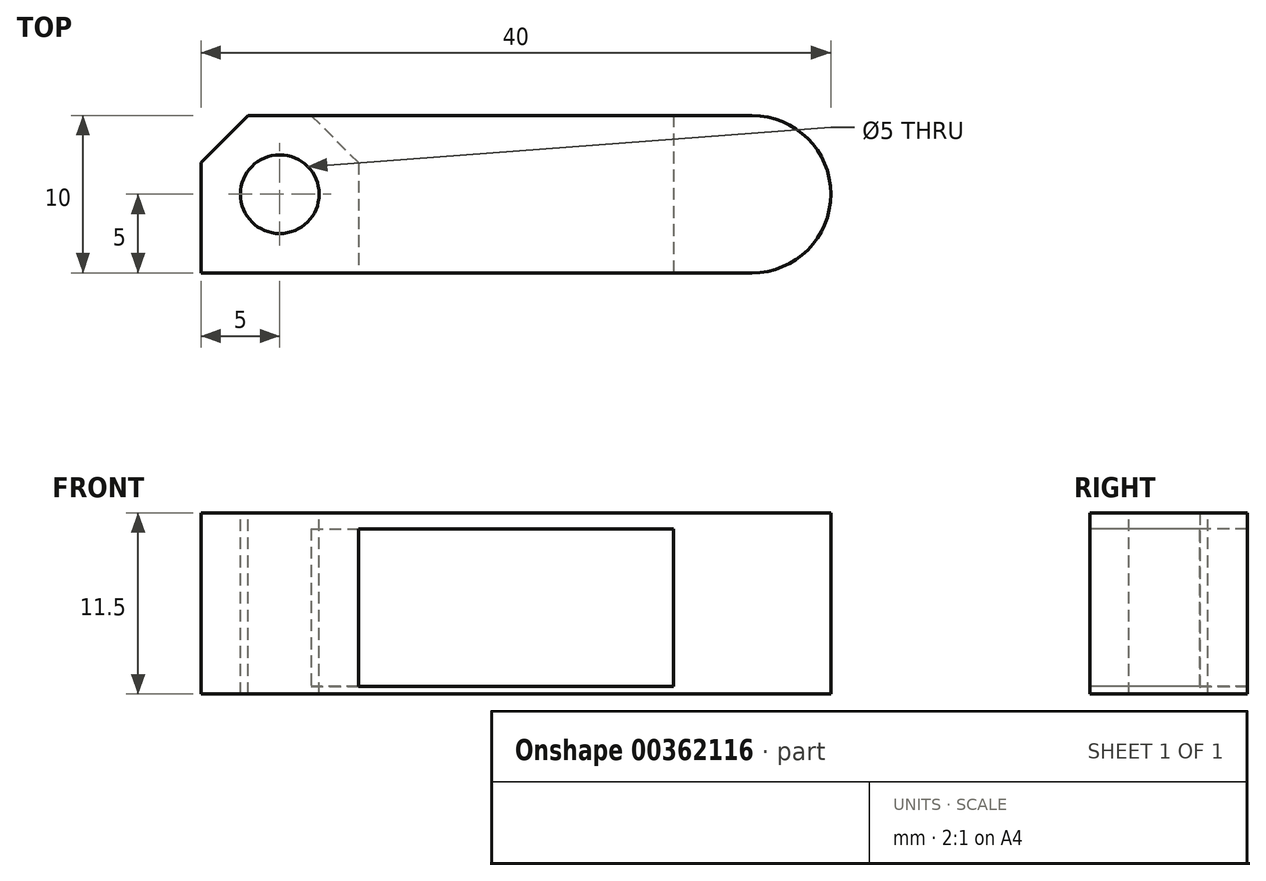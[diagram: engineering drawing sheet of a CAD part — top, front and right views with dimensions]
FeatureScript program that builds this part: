
annotation { "Feature Type Name" : "Feature", "Feature Type Description" : "" }
export const myFeature = defineFeature(function(context is Context, id is Id, definition is map)
    precondition{}
    {
        {
            var Q0;
            Q0=qCreatedBy(makeId("Top.planeOp"),FACE);
            var sketch = newSketch(context, id + "F0", { "sketchPlane" : qUnion([Q0])});
            skLineSegment(sketch, "E0.bottom", {"start": v(-20, 5) * mm, "end": v(20, 5) * mm});
            skLineSegment(sketch, "E0.top", {"start": v(-20, -5) * mm, "end": v(20, -5) * mm});
            skLineSegment(sketch, "E0.left", {"start": v(-20, 5) * mm, "end": v(-20, -5) * mm});
            skLineSegment(sketch, "E0.right", {"start": v(20, 5) * mm, "end": v(20, -5) * mm});
            skPoint(sketch, "E0.middle", {"position": v(0, 0) * mm});
            skSolve(sketch);
        }
        {
            var Q0;
            Q0=makeQuery(id+"F0.imprint","IMPRINT",FACE,{"disambiguationData":[TD([[makeQuery(id+"F0.imprint","IMPRINT",EDGE,{"derivedFrom":sQuery(id+"F0.wireOp",EDGE,"E0.bottom")}),-1.0]])]});
            extrude(context, id + "F1", {"entities" : qUnion([Q0]), "depth" : 0.5 * mm});
        }
        {
            var Q0;
            Q0=makeQuery(id+"F1.opExtrude","CAP_FACE",FACE,{"disambiguationData":[OSD([sQuery(id+"F0.wireOp",EDGE,"E0.bottom"),sQuery(id+"F0.wireOp",EDGE,"E0.top"),sQuery(id+"F0.wireOp",EDGE,"E0.left"),sQuery(id+"F0.wireOp",EDGE,"E0.right")])],"isStart":false});
            var sketch = newSketch(context, id + "F2", { "sketchPlane" : qUnion([Q0])});
            skLineSegment(sketch, "E1.bottom", {"start": v(-20, 5) * mm, "end": v(-10, 5) * mm});
            skLineSegment(sketch, "E1.top", {"start": v(-20, -5) * mm, "end": v(-10, -5) * mm});
            skLineSegment(sketch, "E1.left", {"start": v(-20, 5) * mm, "end": v(-20, -5) * mm});
            skLineSegment(sketch, "E1.right", {"start": v(-10, 5) * mm, "end": v(-10, -5) * mm});
            skLineSegment(sketch, "E2.bottom", {"start": v(20, 5) * mm, "end": v(10, 5) * mm});
            skLineSegment(sketch, "E2.top", {"start": v(20, -5) * mm, "end": v(10, -5) * mm});
            skLineSegment(sketch, "E2.left", {"start": v(20, 5) * mm, "end": v(20, -5) * mm});
            skLineSegment(sketch, "E2.right", {"start": v(10, 5) * mm, "end": v(10, -5) * mm});
            skSolve(sketch);
        }
        {
            var Q0;
            Q0=makeQuery(id+"F2.imprint","IMPRINT",FACE,{"disambiguationData":[TD([[makeQuery(id+"F2.imprint","IMPRINT",EDGE,{"derivedFrom":sQuery(id+"F2.wireOp",EDGE,"E1.bottom")}),-1.0]])]});
            var Q1;
            Q1=makeQuery(id+"F2.imprint","IMPRINT",FACE,{"disambiguationData":[TD([[makeQuery(id+"F2.imprint","IMPRINT",EDGE,{"derivedFrom":sQuery(id+"F2.wireOp",EDGE,"E2.bottom")}),-1.0]])]});
            extrude(context, id + "F3", {"entities" : qUnion([Q0, Q1]), "operationType" : NewBodyOperationType.ADD, "depth" : 10 * mm});
        }
        {
            var Q0;
            Q0=makeQuery(id+"F3.opExtrude","CAP_FACE",FACE,{"disambiguationData":[OSD([sQuery(id+"F2.wireOp",EDGE,"E1.bottom"),sQuery(id+"F2.wireOp",EDGE,"E1.top"),sQuery(id+"F2.wireOp",EDGE,"E1.left"),sQuery(id+"F2.wireOp",EDGE,"E1.right")])],"isStart":false});
            var sketch = newSketch(context, id + "F4", { "sketchPlane" : qUnion([Q0])});
            skLineSegment(sketch, "E3.bottom", {"start": v(-20, -5) * mm, "end": v(20, -5) * mm});
            skLineSegment(sketch, "E3.top", {"start": v(-20, 5) * mm, "end": v(20, 5) * mm});
            skLineSegment(sketch, "E3.left", {"start": v(-20, -5) * mm, "end": v(-20, 5) * mm});
            skLineSegment(sketch, "E3.right", {"start": v(20, -5) * mm, "end": v(20, 5) * mm});
            skSolve(sketch);
        }
        {
            var Q0;
            {var subQ0=sQuery(id+"F4.wireOp",EDGE,"E3.left");Q0=makeQuery(id+"F4.imprint","IMPRINT",FACE,{"disambiguationData":[TD([[makeQuery(id+"F4.imprint","IMPRINT",EDGE,{"derivedFrom":subQ0}),1.0]])]});}
            var Q1;
            {var subQ2=sQuery(id+"F4.wireOp",EDGE,"E3.right");Q1=makeQuery(id+"F4.imprint","IMPRINT",FACE,{"disambiguationData":[TD([[makeQuery(id+"F4.imprint","IMPRINT",EDGE,{"derivedFrom":subQ2}),1.0]])]});}
            extrude(context, id + "F5", {"entities" : qUnion([Q0, Q1]), "operationType" : NewBodyOperationType.ADD, "depth" : 1 * mm});
        }
        {
            var Q0;
            Q0=makeQuery(id+"F5.boolean.opBoolean","MERGE",EDGE,{"derivedFrom":[makeQuery(id+"F3.boolean.opBoolean","MERGE",EDGE,{"derivedFrom":[makeQuery(id+"F1.opExtrude","SWEPT_EDGE",EDGE,{"disambiguationData":[OSD([sQuery(id+"F0.wireOp",EDGE,"E0.top"),sQuery(id+"F0.wireOp",EDGE,"E0.right")])]}),makeQuery(id+"F3.opExtrude","SWEPT_EDGE",EDGE,{"disambiguationData":[OSD([sQuery(id+"F2.wireOp",EDGE,"E2.top"),sQuery(id+"F2.wireOp",EDGE,"E2.left")])]})]}),makeQuery(id+"F5.opExtrude","SWEPT_EDGE",EDGE,{"disambiguationData":[OSD([sQuery(id+"F4.wireOp",EDGE,"E3.bottom"),sQuery(id+"F4.wireOp",EDGE,"E3.right")])]})]});
            var Q1;
            Q1=makeQuery(id+"F5.boolean.opBoolean","MERGE",EDGE,{"derivedFrom":[makeQuery(id+"F3.boolean.opBoolean","MERGE",EDGE,{"derivedFrom":[makeQuery(id+"F1.opExtrude","SWEPT_EDGE",EDGE,{"disambiguationData":[OSD([sQuery(id+"F0.wireOp",EDGE,"E0.bottom"),sQuery(id+"F0.wireOp",EDGE,"E0.right")])]}),makeQuery(id+"F3.opExtrude","SWEPT_EDGE",EDGE,{"disambiguationData":[OSD([sQuery(id+"F2.wireOp",EDGE,"E2.bottom"),sQuery(id+"F2.wireOp",EDGE,"E2.left")])]})]}),makeQuery(id+"F5.opExtrude","SWEPT_EDGE",EDGE,{"disambiguationData":[OSD([sQuery(id+"F4.wireOp",EDGE,"E3.top"),sQuery(id+"F4.wireOp",EDGE,"E3.right")])]})]});
            fillet(context, id + "F6", {"entities" : qUnion([Q0, Q1]), "radius" : 5 * mm, "tangentPropagation" : true, "allowEdgeOverflow" : false});
        }
        {
            var Q0;
            Q0=makeQuery(id+"F5.opExtrude","CAP_FACE",FACE,{"disambiguationData":[OSD([sQuery(id+"F4.wireOp",EDGE,"E3.bottom"),sQuery(id+"F4.wireOp",EDGE,"E3.top"),sQuery(id+"F4.wireOp",EDGE,"E3.left"),sQuery(id+"F4.wireOp",EDGE,"E3.right")])],"isStart":false});
            var sketch = newSketch(context, id + "F7", { "sketchPlane" : qUnion([Q0])});
            skCircle(sketch, "E4", {"center": v(-15, 0) * mm, "radius": 2.5 * mm});
            skSolve(sketch);
        }
        {
            var Q0;
            Q0=makeQuery(id+"F7.imprint","IMPRINT",FACE,{"disambiguationData":[TD([[makeQuery(id+"F7.imprint","IMPRINT",EDGE,{"derivedFrom":sQuery(id+"F7.wireOp",EDGE,"E4")}),1.0]])]});
            extrude(context, id + "F8", {"entities" : qUnion([Q0]), "operationType" : NewBodyOperationType.REMOVE, "oppositeDirection" : true, "depth" : 25 * mm});
        }
        {
            var Q0;
            Q0=makeQuery(id+"F5.boolean.opBoolean","MERGE",EDGE,{"derivedFrom":[makeQuery(id+"F3.boolean.opBoolean","MERGE",EDGE,{"derivedFrom":[makeQuery(id+"F1.opExtrude","SWEPT_EDGE",EDGE,{"disambiguationData":[OSD([sQuery(id+"F0.wireOp",EDGE,"E0.bottom"),sQuery(id+"F0.wireOp",EDGE,"E0.left")])]}),makeQuery(id+"F3.opExtrude","SWEPT_EDGE",EDGE,{"disambiguationData":[OSD([sQuery(id+"F2.wireOp",EDGE,"E1.bottom"),sQuery(id+"F2.wireOp",EDGE,"E1.left")])]})]}),makeQuery(id+"F5.opExtrude","SWEPT_EDGE",EDGE,{"disambiguationData":[OSD([sQuery(id+"F4.wireOp",EDGE,"E3.top"),sQuery(id+"F4.wireOp",EDGE,"E3.left")])]})]});
            var Q1;
            Q1=makeQuery(id+"F3.opExtrude","SWEPT_EDGE",EDGE,{"disambiguationData":[OSD([sQuery(id+"F0.wireOp",EDGE,"E0.bottom"),sQuery(id+"F2.wireOp",EDGE,"E1.bottom"),sQuery(id+"F2.wireOp",EDGE,"E1.right")])]});
            chamfer(context, id + "F9", {"entities" : qUnion([Q0, Q1]), "width" : 3 * mm, "tangentPropagation" : true});
        }
    });
